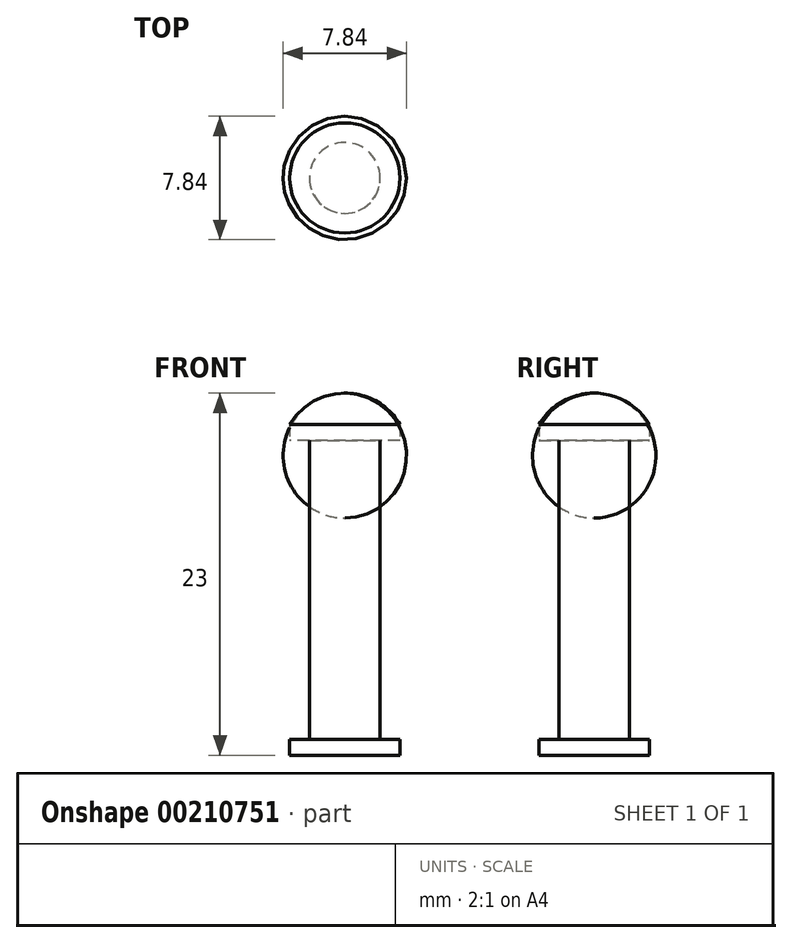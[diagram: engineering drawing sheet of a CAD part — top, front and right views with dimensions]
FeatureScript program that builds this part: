
annotation { "Feature Type Name" : "Feature", "Feature Type Description" : "" }
export const myFeature = defineFeature(function(context is Context, id is Id, definition is map)
    precondition{}
    {
        {
            var Q0;
            Q0=qCreatedBy(makeId("Top.planeOp"),FACE);
            var sketch = newSketch(context, id + "F0", { "sketchPlane" : qUnion([Q0])});
            skCircle(sketch, "E0", {"center": v(0, 0) * mm, "radius": 2.25 * mm});
            skSolve(sketch);
        }
        {
            var Q0;
            Q0 = qSketchRegion(id + "F0", true);
            extrude(context, id + "F1", {"entities" : qUnion([Q0]), "depth" : 20 * mm});
        }
        {
            var Q0;
            Q0=makeQuery(id+"F1.opExtrude","CAP_FACE",FACE,{"disambiguationData":[OSD([sQuery(id+"F0.wireOp",EDGE,"E0")])],"isStart":true});
            var sketch = newSketch(context, id + "F2", { "sketchPlane" : qUnion([Q0])});
            skCircle(sketch, "E1", {"center": v(0, 0) * mm, "radius": 3.5 * mm});
            skSolve(sketch);
        }
        {
            var Q0;
            Q0 = qSketchRegion(id + "F2", true);
            extrude(context, id + "F3", {"entities" : qUnion([Q0]), "operationType" : NewBodyOperationType.ADD, "oppositeDirection" : true, "depth" : 1 * mm});
        }
        {
            var Q0;
            Q0=makeQuery(id+"F1.opExtrude","CAP_FACE",FACE,{"disambiguationData":[OSD([sQuery(id+"F0.wireOp",EDGE,"E0")])],"isStart":false});
            var sketch = newSketch(context, id + "F4", { "sketchPlane" : qUnion([Q0])});
            skCircle(sketch, "E2", {"center": v(0, 0) * mm, "radius": 3.5 * mm});
            skSolve(sketch);
        }
        {
            var Q0;
            Q0 = qSketchRegion(id + "F4", true);
            extrude(context, id + "F5", {"entities" : qUnion([Q0]), "operationType" : NewBodyOperationType.ADD, "depth" : 1 * mm});
        }
        {
            var Q0;
            Q0=qCreatedBy(makeId("Front.planeOp"),FACE);
            var sketch = newSketch(context, id + "F6", { "sketchPlane" : qUnion([Q0])});
            skLineSegment(sketch, "E3", {"start": v(0, -3.45) * mm, "end": v(0, 25.88) * mm, "construction": true});
            skArc(sketch, "E4", {"start": v(0, 23) * mm, "mid": v(-2.02, 22.48) * mm, "end": v(-3.5, 21) * mm});
            skLineSegment(sketch, "E5", {"start": v(0, 23) * mm, "end": v(0, 21) * mm});
            skLineSegment(sketch, "E6", {"start": v(0, 21) * mm, "end": v(-3.5, 21) * mm});
            skSolve(sketch);
        }
        {
            var Q0;
            Q0=makeQuery(id+"F6.imprint","IMPRINT",FACE,{"disambiguationData":[TD([[makeQuery(id+"F6.imprint","IMPRINT",EDGE,{"derivedFrom":sQuery(id+"F6.wireOp",EDGE,"E4")}),1.0]])]});
            var Q1;
            Q1=sQuery(id+"F6.wireOp",EDGE,"E3");
            revolve(context, id + "F7", {"operationType" : NewBodyOperationType.ADD, "entities" : qUnion([Q0]), "axis" : qUnion([Q1]), "revolveType" : RevolveType.FULL});
        }
    });
